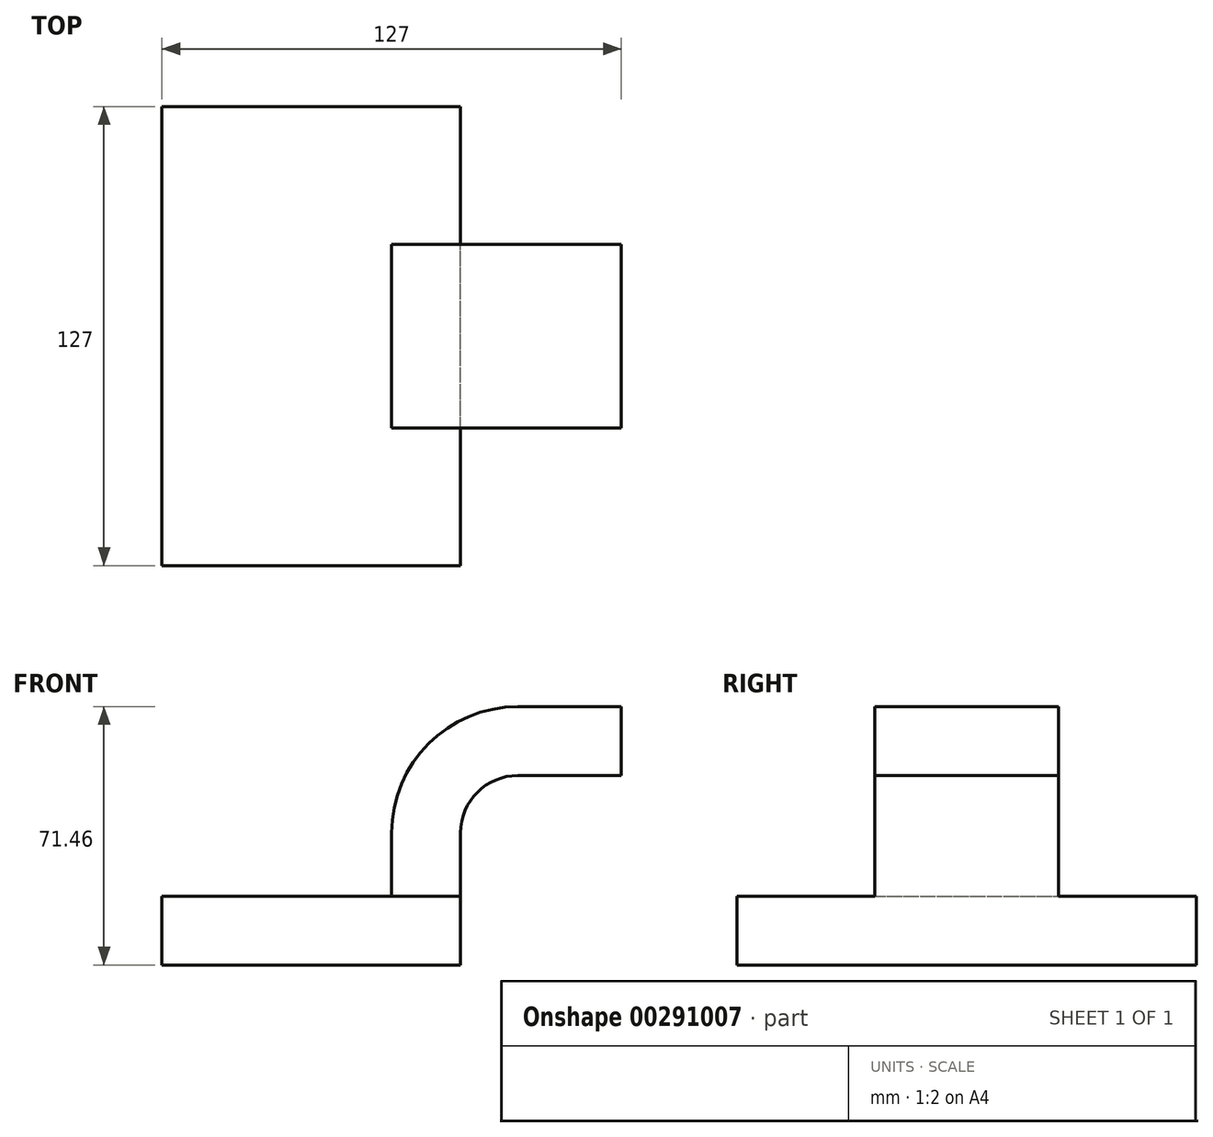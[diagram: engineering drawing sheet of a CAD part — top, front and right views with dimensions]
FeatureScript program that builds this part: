
annotation { "Feature Type Name" : "Feature", "Feature Type Description" : "" }
export const myFeature = defineFeature(function(context is Context, id is Id, definition is map)
    precondition{}
    {
        {
            var Q0;
            Q0=qCreatedBy(makeId("Front.planeOp"),FACE);
            var sketch = newSketch(context, id + "F0", { "sketchPlane" : qUnion([Q0])});
            skLineSegment(sketch, "E0.bottom", {"start": v(41.28, 9.53) * mm, "end": v(-41.28, 9.53) * mm});
            skLineSegment(sketch, "E0.top", {"start": v(41.28, -9.53) * mm, "end": v(-41.28, -9.53) * mm});
            skLineSegment(sketch, "E0.left", {"start": v(41.27, 9.53) * mm, "end": v(41.28, -9.53) * mm});
            skLineSegment(sketch, "E0.right", {"start": v(-41.28, 9.53) * mm, "end": v(-41.27, -9.53) * mm});
            skPoint(sketch, "E0.middle", {"position": v(0, 0) * mm});
            skLineSegment(sketch, "E1.bottom", {"start": v(60.33, 66.67) * mm, "end": v(111.12, 66.67) * mm});
            skLineSegment(sketch, "E1.top", {"start": v(60.33, 38.1) * mm, "end": v(111.12, 38.1) * mm});
            skLineSegment(sketch, "E1.left", {"start": v(60.33, 66.67) * mm, "end": v(60.33, 38.1) * mm});
            skLineSegment(sketch, "E1.right", {"start": v(111.12, 66.67) * mm, "end": v(111.12, 38.1) * mm});
            skPoint(sketch, "E1.middle", {"position": v(85.72, 52.39) * mm});
            skLineSegment(sketch, "E2", {"start": v(41.28, 9.53) * mm, "end": v(41.28, 27) * mm});
            skArc(sketch, "E3", {"start": v(41.27, 27) * mm, "mid": v(45.92, 38.23) * mm, "end": v(57.15, 42.88) * mm});
            skLineSegment(sketch, "E4", {"start": v(57.15, 42.88) * mm, "end": v(85.72, 42.88) * mm});
            skLineSegment(sketch, "E5.0", {"start": v(57.15, 61.93) * mm, "end": v(85.72, 61.93) * mm});
            skArc(sketch, "E5.1", {"start": v(22.23, 27) * mm, "mid": v(32.45, 51.7) * mm, "end": v(57.15, 61.93) * mm});
            skLineSegment(sketch, "E5.2", {"start": v(22.22, 9.53) * mm, "end": v(22.22, 27) * mm});
            skLineSegment(sketch, "E6", {"start": v(85.72, 38.1) * mm, "end": v(85.72, 66.67) * mm});
            skFitSpline(sketch, "E7", {"points": [v(-41.28, 9.52) * mm, v(57.15, 61.93) * mm], "startDerivative": vector(1.3, 142.94) * mm, "endDerivative": vector(113.93, -11.27) * mm});
            skSolve(sketch);
        }
        {
            var Q0;
            Q0=makeQuery(id+"F0.imprint","IMPRINT",FACE,{"disambiguationData":[TD([[makeQuery(id+"F0.imprint","IMPRINT",EDGE,{"derivedFrom":sQuery(id+"F0.wireOp",EDGE,"E0.top")}),-1.0]])]});
            extrude(context, id + "F1", {"entities" : qUnion([Q0]), "endBound" : BoundingType.SYMMETRIC, "depth" : 127 * mm});
        }
        {
            var Q0;
            {var subQ1=sQuery(id+"F0.wireOp",EDGE,"E2");Q0=makeQuery(id+"F0.imprint","IMPRINT",FACE,{"disambiguationData":[TD([[makeQuery(id+"F0.imprint","IMPRINT",EDGE,{"derivedFrom":subQ1}),1.0]])]});}
            var Q1;
            {var subQ0=sQuery(id+"F0.wireOp",EDGE,"E5.0");var subQ1=sQuery(id+"F0.wireOp",EDGE,"E1.left");var subQ2=makeQuery(id+"F0.imprint","INTERSECT",VERTEX,{"derivedFrom":[subQ1,subQ0]});Q1=makeQuery(id+"F0.imprint","IMPRINT",FACE,{"disambiguationData":[TD([[makeQuery(id+"F0.imprint","IMPRINT",EDGE,{"disambiguationData":[TD([[subQ2,-1.0]])],"derivedFrom":subQ1}),1.0]])]});}
            extrude(context, id + "F2", {"entities" : qUnion([Q0, Q1]), "operationType" : NewBodyOperationType.ADD, "endBound" : BoundingType.SYMMETRIC, "depth" : 50.8 * mm});
        }
        {
            var Q0;
            Q0=makeQuery(id+"F0.imprint","IMPRINT",FACE,{"disambiguationData":[TD([[makeQuery(id+"F0.imprint","IMPRINT",EDGE,{"derivedFrom":sQuery(id+"F0.wireOp",EDGE,"E5.1")}),1.0]])]});
            extrude(context, id + "F3", {"entities" : qUnion([Q0]), "operationType" : NewBodyOperationType.ADD, "endBound" : BoundingType.SYMMETRIC, "depth" : 15.88 * mm});
        }
    });
